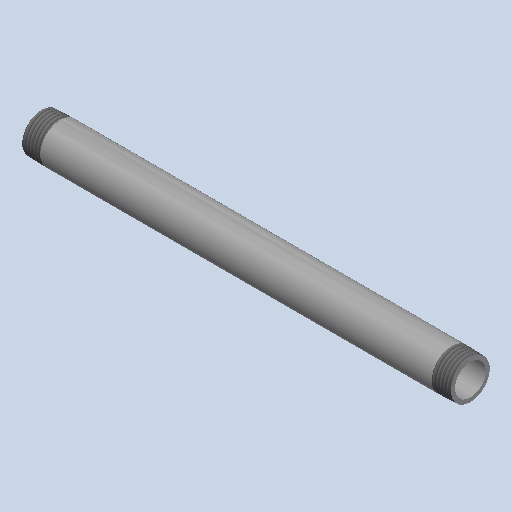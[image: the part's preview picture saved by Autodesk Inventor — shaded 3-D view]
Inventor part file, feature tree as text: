
AUTODESK INVENTOR PART (.ipt)
format: ipt  version: 2025 (Build 290162000, 162)  size: 165,888 bytes
history: native  units: mm (DEFAULTED — no unit token found)
features: other x8, revolve x1
ambient origin geometry x8: Origin, YZ Plane, XZ Plane, XY Plane, X Axis, Y Axis, Z Axis, Center Point
bodies: Solid1 (feature_tree)
feature tree (9):
  revolve  "Revolution1"  [1 undecoded]
  other  "Work Axis1"
  other  "Work Point5"
  other  "Work Axis2"
  other  "Work Point6"
  other  "Work Axis3"
  other  "Work Axis4"
  other  "Work Point7"
  other  "Work Point8"
note: 1 required parameter value undecoded (feature->parameter linkage not recoverable at this tier; creation-order binding heuristic only, values carry confidence <= 0.55)
